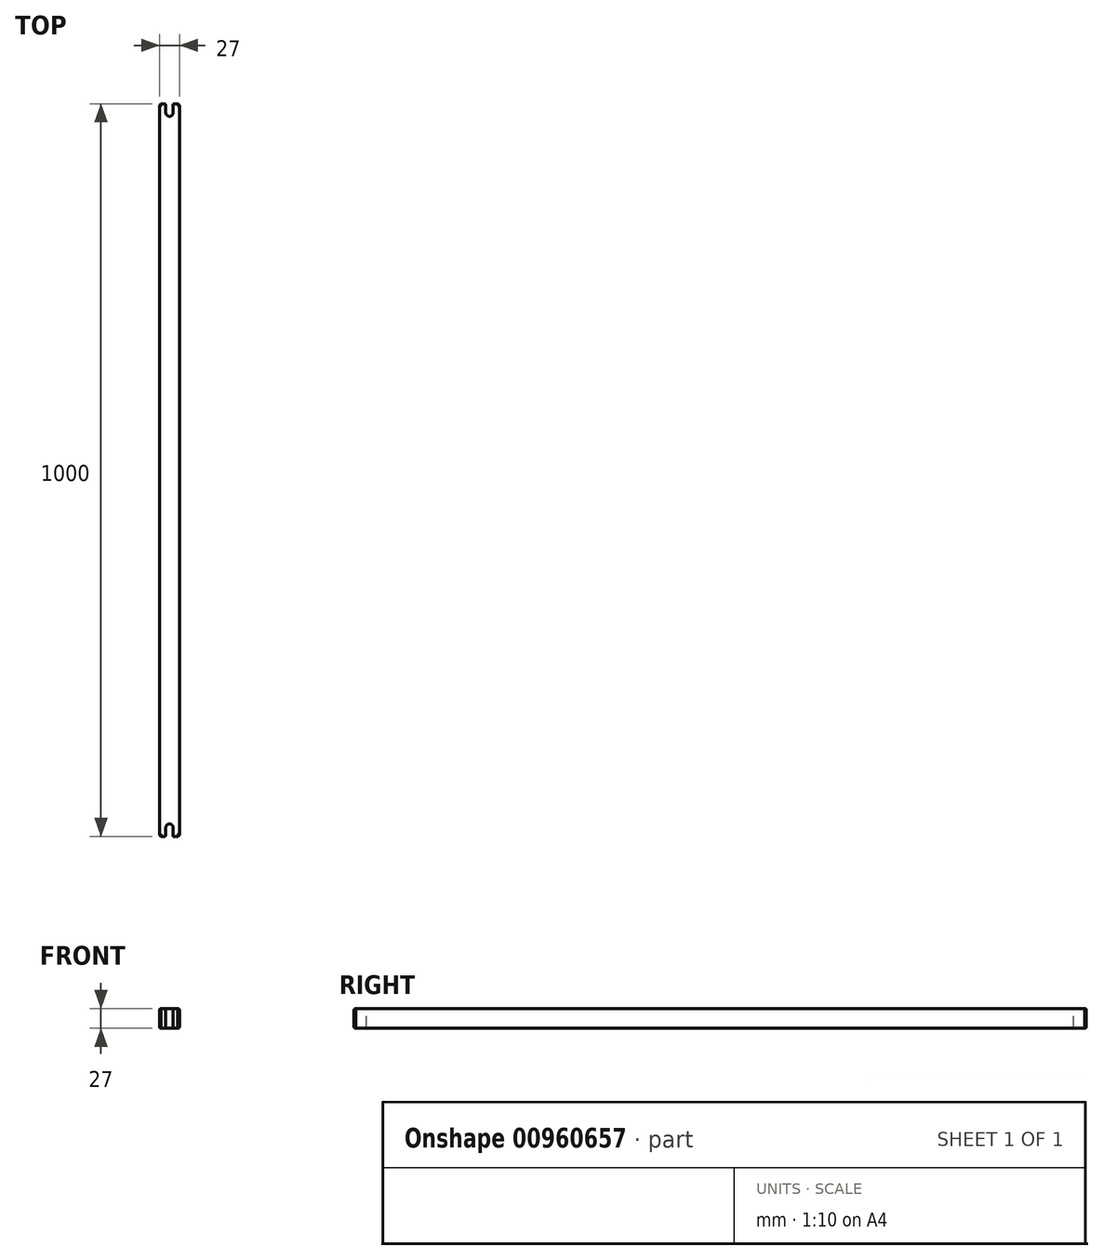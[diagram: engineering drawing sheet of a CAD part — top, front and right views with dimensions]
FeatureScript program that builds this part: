
annotation { "Feature Type Name" : "Feature", "Feature Type Description" : "" }
export const myFeature = defineFeature(function(context is Context, id is Id, definition is map)
    precondition{}
    {
        {
            var Q0;
            Q0=qCreatedBy(makeId("Front.planeOp"),FACE);
            var sketch = newSketch(context, id + "F0", { "sketchPlane" : qUnion([Q0])});
            skLineSegment(sketch, "E0.bottom", {"start": v(0, 0) * mm, "end": v(27, 0) * mm});
            skLineSegment(sketch, "E0.top", {"start": v(0, 27) * mm, "end": v(27, 27) * mm});
            skLineSegment(sketch, "E0.left", {"start": v(0, 0) * mm, "end": v(0, 27) * mm});
            skLineSegment(sketch, "E0.right", {"start": v(27, 0) * mm, "end": v(27, 27) * mm});
            skSolve(sketch);
        }
        {
            var Q0;
            Q0=makeQuery(id+"F0.imprint","IMPRINT",FACE,{"disambiguationData":[TD([[makeQuery(id+"F0.imprint","IMPRINT",EDGE,{"derivedFrom":sQuery(id+"F0.wireOp",EDGE,"E0.bottom")}),1.0]])]});
            extrude(context, id + "F1", {"entities" : qUnion([Q0]), "endBound" : BoundingType.SYMMETRIC, "depth" : 1000 * mm, "offsetDistance" : 25 * mm});
        }
        {
            var Q0;
            Q0=makeQuery(id+"F1.opExtrude","SWEPT_FACE",FACE,{"disambiguationData":[OSD([sQuery(id+"F0.wireOp",EDGE,"E0.top")])]});
            var sketch = newSketch(context, id + "F2", { "sketchPlane" : qUnion([Q0])});
            skArc(sketch, "E1", {"start": v(18.5, -488) * mm, "mid": v(13.5, -483) * mm, "end": v(8.5, -488) * mm});
            skPoint(sketch, "E1.centerSnap0", {"position": v(13.5, -500) * mm});
            skLineSegment(sketch, "E2.top", {"start": v(8.5, -500) * mm, "end": v(18.5, -500) * mm});
            skLineSegment(sketch, "E2.left", {"start": v(8.5, -488) * mm, "end": v(8.5, -500) * mm});
            skLineSegment(sketch, "E2.right", {"start": v(18.5, -488) * mm, "end": v(18.5, -500) * mm});
            skArc(sketch, "E3.MirrorCS", {"start": v(18.5, 488) * mm, "mid": v(13.5, 483) * mm, "end": v(8.5, 488) * mm});
            skLineSegment(sketch, "E4.MirrorCS", {"start": v(8.5, 500) * mm, "end": v(18.5, 500) * mm});
            skPoint(sketch, "E5.MirrorP", {"position": v(13.5, 500) * mm});
            skLineSegment(sketch, "E6.MirrorCS", {"start": v(18.5, 488) * mm, "end": v(18.5, 500) * mm});
            skLineSegment(sketch, "E7.MirrorCS", {"start": v(8.5, 488) * mm, "end": v(8.5, 500) * mm});
            skSolve(sketch);
        }
        {
            var Q0;
            Q0=makeQuery(id+"F2.imprint","IMPRINT",FACE,{"disambiguationData":[TD([[makeQuery(id+"F2.imprint","IMPRINT",EDGE,{"derivedFrom":sQuery(id+"F2.wireOp",EDGE,"E1")}),1.0]])]});
            extrude(context, id + "F3", {"entities" : qUnion([Q0]), "operationType" : NewBodyOperationType.REMOVE, "endBound" : BoundingType.THROUGH_ALL, "oppositeDirection" : true, "depth" : 25 * mm, "offsetDistance" : 25 * mm});
        }
        {
            var Q0;
            Q0=qSketchRegion(id+"F2",true);
            extrude(context, id + "F4", {"entities" : qUnion([Q0]), "operationType" : NewBodyOperationType.REMOVE, "endBound" : BoundingType.THROUGH_ALL, "oppositeDirection" : true, "depth" : 25 * mm, "offsetDistance" : 25 * mm});
        }
        {
            var Q0;
            Q0=makeQuery(id+"F1.opExtrude","CAP_EDGE",EDGE,{"disambiguationData":[OSD([sQuery(id+"F0.wireOp",EDGE,"E0.left")])],"isStart":false});
            var Q1;
            Q1=makeQuery(id+"F1.opExtrude","CAP_EDGE",EDGE,{"disambiguationData":[OSD([sQuery(id+"F0.wireOp",EDGE,"E0.right")])],"isStart":false});
            var Q2;
            Q2=makeQuery(id+"F1.opExtrude","CAP_EDGE",EDGE,{"disambiguationData":[OSD([sQuery(id+"F0.wireOp",EDGE,"E0.left")])],"isStart":true});
            var Q3;
            Q3=makeQuery(id+"F1.opExtrude","CAP_EDGE",EDGE,{"disambiguationData":[OSD([sQuery(id+"F0.wireOp",EDGE,"E0.right")])],"isStart":true});
            chamfer(context, id + "F5", {"entities" : qUnion([Q0, Q1, Q2, Q3]), "width" : 2 * mm, "tangentPropagation" : true});
        }
        {
            var Q0;
            Q0=makeQuery(id+"F1.opExtrude","SWEPT_FACE",FACE,{"disambiguationData":[OSD([sQuery(id+"F0.wireOp",EDGE,"E0.top")])]});
            var Q1;
            Q1=makeQuery(id+"F1.opExtrude","SWEPT_FACE",FACE,{"disambiguationData":[OSD([sQuery(id+"F0.wireOp",EDGE,"E0.bottom")])]});
            var Q2;
            Q2=makeQuery(id+"F4.boolean.opBoolean","COPY",EDGE,{"derivedFrom":makeQuery(id+"F4.opExtrude","SWEPT_EDGE",EDGE,{"disambiguationData":[OSD([sQuery(id+"F0.wireOp",EDGE,"E0.top"),sQuery(id+"F2.wireOp",EDGE,"E4.MirrorCS"),sQuery(id+"F2.wireOp",EDGE,"E6.MirrorCS")])]})});
            var Q3;
            Q3=makeQuery(id+"F4.boolean.opBoolean","COPY",EDGE,{"derivedFrom":makeQuery(id+"F4.opExtrude","SWEPT_EDGE",EDGE,{"disambiguationData":[OSD([sQuery(id+"F0.wireOp",EDGE,"E0.top"),sQuery(id+"F2.wireOp",EDGE,"E4.MirrorCS"),sQuery(id+"F2.wireOp",EDGE,"E7.MirrorCS")])]})});
            var Q4;
            Q4=makeQuery(id+"F3.boolean.opBoolean","COPY",EDGE,{"derivedFrom":makeQuery(id+"F3.opExtrude","SWEPT_EDGE",EDGE,{"disambiguationData":[OSD([sQuery(id+"F0.wireOp",EDGE,"E0.top"),sQuery(id+"F2.wireOp",EDGE,"E2.top"),sQuery(id+"F2.wireOp",EDGE,"E2.right")])]})});
            var Q5;
            Q5=makeQuery(id+"F3.boolean.opBoolean","COPY",EDGE,{"derivedFrom":makeQuery(id+"F3.opExtrude","SWEPT_EDGE",EDGE,{"disambiguationData":[OSD([sQuery(id+"F0.wireOp",EDGE,"E0.top"),sQuery(id+"F2.wireOp",EDGE,"E2.top"),sQuery(id+"F2.wireOp",EDGE,"E2.left")])]})});
            fillet(context, id + "F6", {"entities" : qUnion([Q0, Q1, Q2, Q3, Q4, Q5]), "radius" : 2 * mm, "tangentPropagation" : true, "allowEdgeOverflow" : false});
        }
    });
